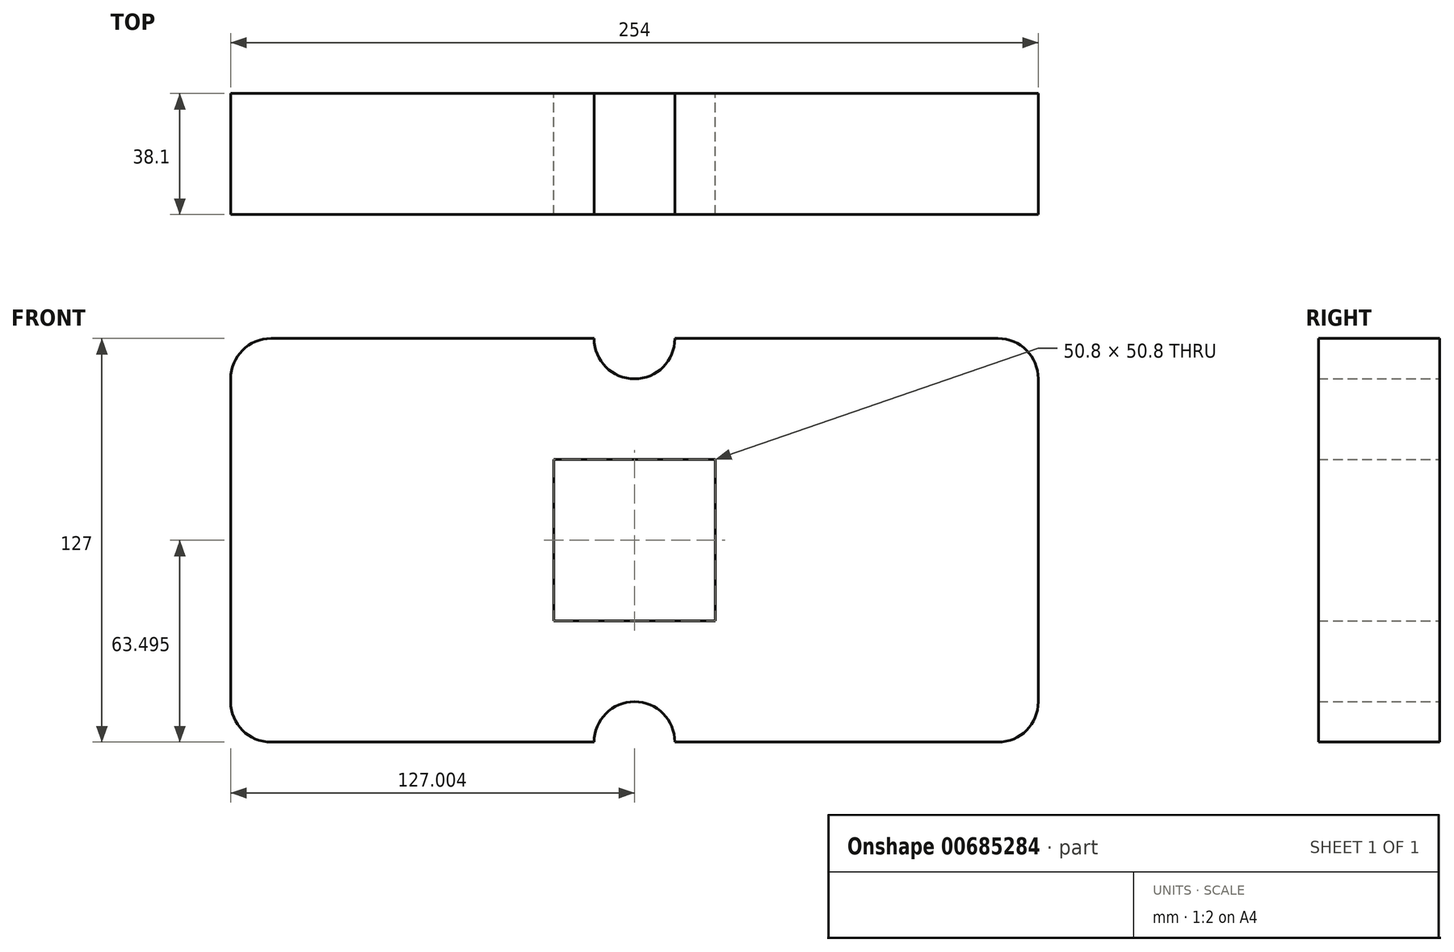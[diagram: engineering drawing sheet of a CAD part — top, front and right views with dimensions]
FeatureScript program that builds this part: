
annotation { "Feature Type Name" : "Feature", "Feature Type Description" : "" }
export const myFeature = defineFeature(function(context is Context, id is Id, definition is map)
    precondition{}
    {
        {
            var Q0;
            Q0=qCreatedBy(makeId("Front.planeOp"),FACE);
            var sketch = newSketch(context, id + "F0", { "sketchPlane" : qUnion([Q0])});
            skLineSegment(sketch, "E0.bottom", {"start": v(-112.46, 39.86) * mm, "end": v(-10.86, 39.86) * mm});
            skLineSegment(sketch, "E0.top", {"start": v(-112.46, -87.14) * mm, "end": v(-10.86, -87.14) * mm});
            skLineSegment(sketch, "E0.left", {"start": v(-125.16, 27.16) * mm, "end": v(-125.16, -74.44) * mm});
            skLineSegment(sketch, "E0.right", {"start": v(128.84, 27.16) * mm, "end": v(128.84, -74.44) * mm});
            skPoint(sketch, "E1.visualSharp", {"position": v(-125.16, 39.86) * mm});
            skArc(sketch, "E1.filletArc", {"start": v(-112.46, 39.86) * mm, "mid": v(-121.44, 36.14) * mm, "end": v(-125.16, 27.16) * mm});
            skPoint(sketch, "E2.visualSharp", {"position": v(128.84, 39.86) * mm});
            skArc(sketch, "E2.filletArc", {"start": v(128.84, 27.16) * mm, "mid": v(125.12, 36.14) * mm, "end": v(116.14, 39.86) * mm});
            skPoint(sketch, "E3.visualSharp", {"position": v(128.84, -87.14) * mm});
            skArc(sketch, "E3.filletArc", {"start": v(116.14, -87.14) * mm, "mid": v(125.12, -83.42) * mm, "end": v(128.84, -74.44) * mm});
            skPoint(sketch, "E4.visualSharp", {"position": v(-125.16, -87.14) * mm});
            skArc(sketch, "E4.filletArc", {"start": v(-125.16, -74.44) * mm, "mid": v(-121.44, -83.42) * mm, "end": v(-112.46, -87.14) * mm});
            skArc(sketch, "E5", {"start": v(-10.86, 39.86) * mm, "mid": v(1.84, 27.16) * mm, "end": v(14.54, 39.86) * mm});
            skArc(sketch, "E6", {"start": v(14.54, -87.14) * mm, "mid": v(1.84, -74.44) * mm, "end": v(-10.86, -87.14) * mm});
            skLineSegment(sketch, "E7.trimOffspring", {"start": v(14.54, 39.86) * mm, "end": v(116.14, 39.86) * mm});
            skLineSegment(sketch, "E8.trimOffspring", {"start": v(14.54, -87.14) * mm, "end": v(116.14, -87.14) * mm});
            skLineSegment(sketch, "E9", {"start": v(-23.56, 1.76) * mm, "end": v(27.24, 1.76) * mm});
            skLineSegment(sketch, "E10", {"start": v(27.24, 1.76) * mm, "end": v(27.24, -49.04) * mm});
            skLineSegment(sketch, "E11", {"start": v(27.24, -49.04) * mm, "end": v(-24.33, -49.04) * mm});
            skLineSegment(sketch, "E12", {"start": v(-23.56, 1.76) * mm, "end": v(-23.56, -49.04) * mm});
            skSolve(sketch);
        }
        {
            var Q0;
            Q0 = qSketchRegion(id + "F0", true);
            extrude(context, id + "F1", {"entities" : qUnion([Q0]), "depth" : 38.1 * mm, "offsetDistance" : 25.4 * mm});
        }
    });
